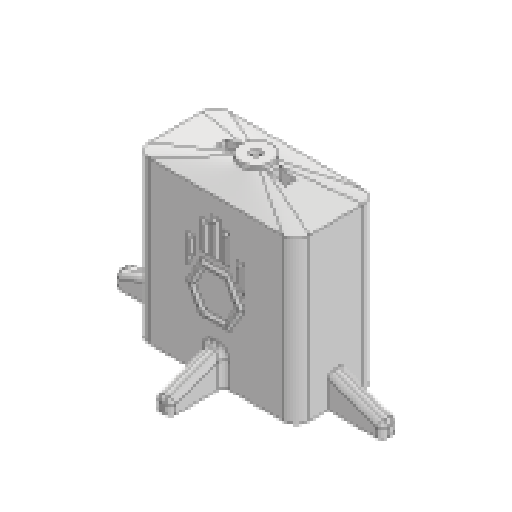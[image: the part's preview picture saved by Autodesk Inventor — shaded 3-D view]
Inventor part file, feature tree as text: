
AUTODESK INVENTOR PART (.ipt)
format: ipt  version: 2025 (Build 290162010, 162A)  size: 456,192 bytes
history: native  units: in
note: dims shown in document units (in); Inventor stores cm internally (conversion verified against a paired STEP export)
features: sketch x10, extrude x9, plane x3, fillet x3, chamfer x2, mirror x2, projected_geometry x2, loft x1, other x1
ambient origin geometry x8: Origin, YZ Plane, XZ Plane, XY Plane, X Axis, Y Axis, Z Axis, Center Point
bodies: Solid1 (feature_tree)
feature tree (33):
  extrude  "Extrusion1"  Depth=0.2in
  plane  "Work Plane1"
  sketch  "Sketch3"  dims[d2=0.08in d3=0.0in d4=0.25in]
  loft  "Loft1"
  extrude  "Extrusion2"  Depth=1.5in
  extrude  "Extrusion3"  TaperAngle=0.0deg  [1 undecoded]
  chamfer  "Chamfer1"  Angle=90.0deg  [1 undecoded]
  plane  "Work Plane2"
  plane  "Work Plane3"
  extrude  "Extrusion4"  Depth=0.2in
  fillet  "Fillet1"  Radius=2.8in
  mirror  "Mirror1"
  extrude  "Extrusion5"  Depth=0.2in
  fillet  "Fillet2"  Radius=0.2in
  mirror  "Mirror2"
  extrude  "Extrusion6"  Depth=0.1374in
  extrude  "Extrusion7"  Depth=0.3in TaperAngle=0.0deg
  chamfer  "Chamfer2"  Distance=0.6in
  extrude  "Extrusion8"  Depth=0.1in
  extrude  "Extrusion9"  Depth=0.1in
  fillet  "Fillet3"  Radius=0.3in
  sketch  "Sketch1"  dims[d0=0.184in d1=0.2in]
  other  "Edges1"
  sketch  "Sketch5"  dims[d5=3.0in d6=1.5in]
  projected_geometry  "Projected Loop1"
  sketch  "Sketch6"  dims[d7=0.25in d8=0.0in d9=90.0deg d10=0.0in d11=90.0deg]
  projected_geometry  "Projected Loop2"
  sketch  "Sketch7"  dims[d12=3.0in d13=0.0in d14=0.2in d15=2.8in d16=0.0in]
  sketch  "Sketch8"  dims[d17=0.2in d18=0.2in d19=0.2in]
  sketch  "Sketch9"  dims[d20=0.55in d21=0.125in d22=45.0deg d23=0.1374in]
  sketch  "Sketch10"  dims[d24=1.0in d25=0.3in d26=0.0in]
  sketch  "Sketch11"  dims[d27=0.1in]
  sketch  "Sketch12"  dims[d28=0.1374in d29=0.6in d30=0.6in d31=1.0in d32=0.3in d33=0.0in d34=0.1in d35=0.07in d36=0.7in d37=0.0in d38=0.538in d39=0.1344in d40=0.1073in d41=0.107in d42=0.1344in d43=0.1344in d44=0.1344in d45=0.1344in d46=0.107in d47=0.5377in d48=0.5377in d49=0.6721in d50=0.1344in d51=0.05in d52=0.0in d53=0.05in d54=0.125in d55=45.0deg d56=0.4in d57=0.6in d58=0.35in d59=1.2in d60=0.0in d61=0.6in d62=0.6in d63=0.3in d64=0.3in d65=0.6in d66=0.3in d67=0.7375in d68=0.0in d69=45.0deg d70=45.0deg d71=0.1in d72=0.1344in d73=0.0672in d74=0.5382in d78=0.1344in]
note: 2 required parameter values undecoded (feature->parameter linkage not recoverable at this tier; creation-order binding heuristic only, values carry confidence <= 0.55)
